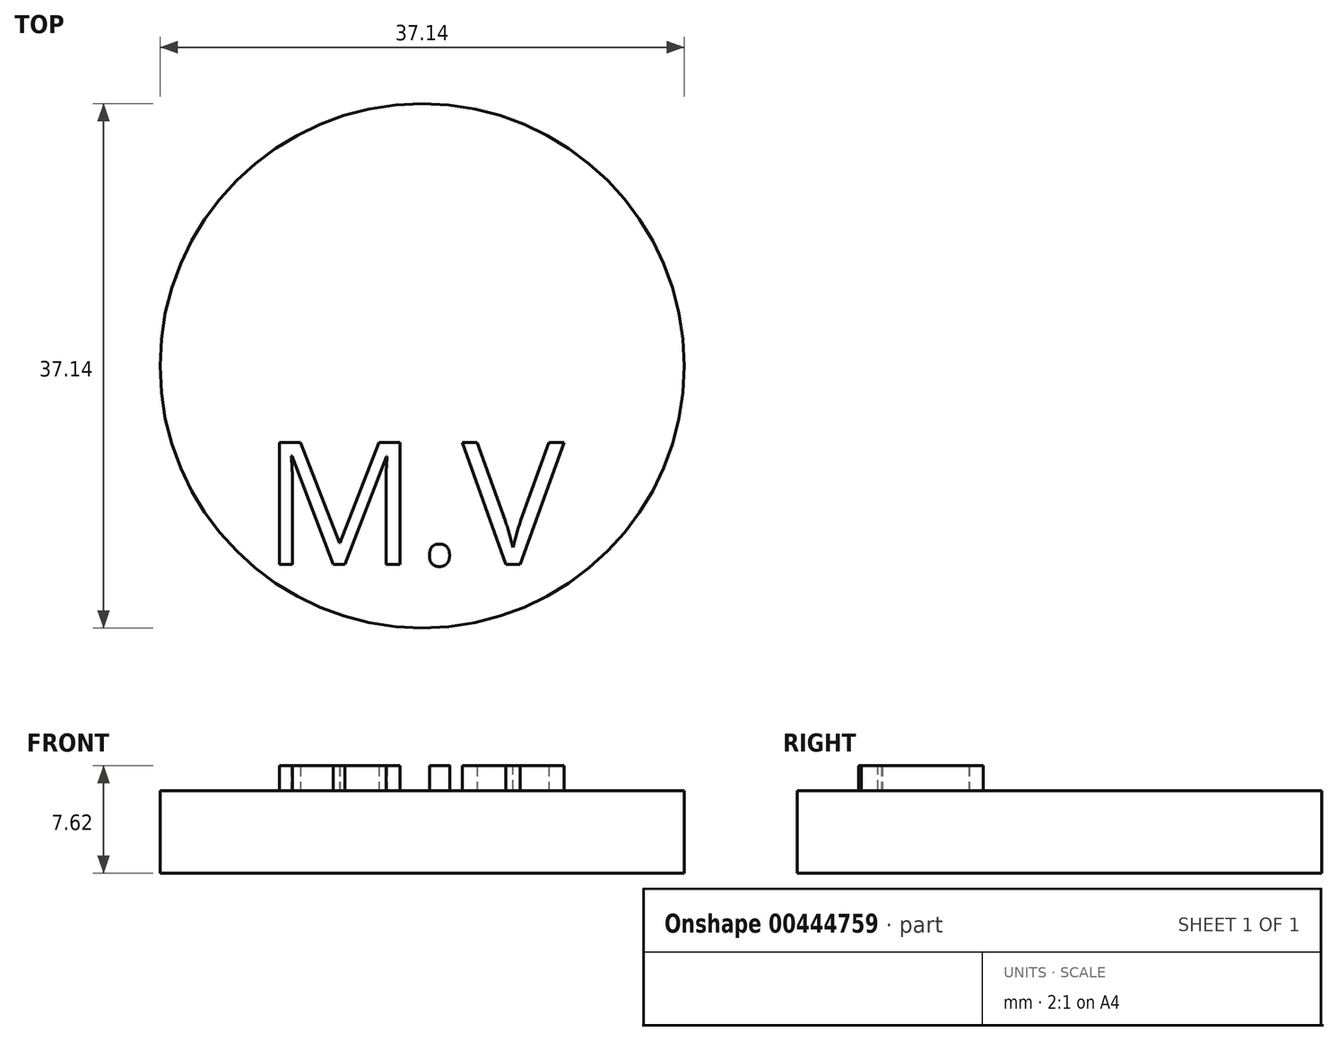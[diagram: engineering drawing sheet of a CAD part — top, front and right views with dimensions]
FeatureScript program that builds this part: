
annotation { "Feature Type Name" : "Feature", "Feature Type Description" : "" }
export const myFeature = defineFeature(function(context is Context, id is Id, definition is map)
    precondition{}
    {
        {
            var Q0;
            Q0=qCreatedBy(makeId("Top.planeOp"),FACE);
            var sketch = newSketch(context, id + "F0", { "sketchPlane" : qUnion([Q0])});
            skLineSegment(sketch, "E0.bottom", {"start": v(38.1, -19.05) * mm, "end": v(-38.1, -19.05) * mm});
            skLineSegment(sketch, "E0.top", {"start": v(38.1, 19.05) * mm, "end": v(-38.1, 19.05) * mm});
            skLineSegment(sketch, "E0.left", {"start": v(38.1, -19.05) * mm, "end": v(38.1, 19.05) * mm});
            skLineSegment(sketch, "E0.right", {"start": v(-38.1, -19.05) * mm, "end": v(-38.1, 19.05) * mm});
            skPoint(sketch, "E0.middle", {"position": v(0, 0) * mm});
            skSolve(sketch);
        }
        {
            var Q0;
            Q0=makeQuery(id+"F0.imprint","IMPRINT",FACE,{"disambiguationData":[TD([[makeQuery(id+"F0.imprint","IMPRINT",EDGE,{"derivedFrom":sQuery(id+"F0.wireOp",EDGE,"E0.bottom")}),-1.0]])]});
            var sketch = newSketch(context, id + "F1", { "sketchPlane" : qUnion([Q0])});
            skCircle(sketch, "E1", {"center": v(0, 0) * mm, "radius": 18.57 * mm});
            skSolve(sketch);
        }
        {
            var Q0;
            Q0=sQuery(id+"F0.wireOp",EDGE,"E0.top");
            var Q1;
            Q1=sQuery(id+"F0.wireOp",EDGE,"E0.right");
            var Q2;
            Q2=sQuery(id+"F0.wireOp",EDGE,"E0.bottom");
            var Q3;
            Q3=sQuery(id+"F0.wireOp",EDGE,"E0.left");
            extrude(context, id + "F2", {"bodyType" : ToolBodyType.SURFACE, "surfaceEntities" : qUnion([Q0, Q1, Q2, Q3]), "endBound" : BoundingType.SYMMETRIC, "depth" : 6.35 * mm});
        }
        {
            var Q0;
            Q0=makeQuery(id+"F1.imprint","IMPRINT",FACE,{"disambiguationData":[TD([[makeQuery(id+"F1.imprint","IMPRINT",EDGE,{"derivedFrom":sQuery(id+"F1.wireOp",EDGE,"E1")}),1.0]])]});
            extrude(context, id + "F3", {"entities" : qUnion([Q0]), "depth" : 5.84 * mm});
        }
        {
            var Q0;
            Q0=makeQuery(id+"F3.opExtrude","CAP_FACE",FACE,{"disambiguationData":[OSD([sQuery(id+"F1.wireOp",EDGE,"E1")])],"isStart":false});
            var sketch = newSketch(context, id + "F4", { "sketchPlane" : qUnion([Q0])});
            skCircle(sketch, "E2", {"center": v(0, 0) * mm, "radius": 6.17 * mm});
            skCircle(sketch, "E3", {"center": v(0, 0) * mm, "radius": 3.28 * mm});
            skSolve(sketch);
        }
        {
            var Q0;
            Q0=sQuery(id+"F4.wireOp",EDGE,"E2");
            var Q1;
            Q1=sQuery(id+"F4.wireOp",EDGE,"E3");
            extrude(context, id + "F5", {"bodyType" : ToolBodyType.SURFACE, "surfaceEntities" : qUnion([Q0, Q1]), "depth" : 2.54 * mm});
        }
        {
            var Q0;
            Q0=makeQuery(id+"F3.opExtrude","CAP_FACE",FACE,{"disambiguationData":[OSD([sQuery(id+"F1.wireOp",EDGE,"E1")])],"isStart":false});
            var sketch = newSketch(context, id + "F6", { "sketchPlane" : qUnion([Q0])});
            skLineSegment(sketch, "E4.bottom", {"start": v(18.47, -1.91) * mm, "end": v(-18.47, -1.91) * mm});
            skLineSegment(sketch, "E4.top", {"start": v(18.47, 1.91) * mm, "end": v(-18.47, 1.91) * mm});
            skLineSegment(sketch, "E4.left", {"start": v(18.47, -1.91) * mm, "end": v(18.47, 1.91) * mm});
            skLineSegment(sketch, "E4.right", {"start": v(-18.47, -1.91) * mm, "end": v(-18.47, 1.91) * mm});
            skPoint(sketch, "E4.middle", {"position": v(0, 0) * mm});
            skSolve(sketch);
        }
        {
            var Q0;
            Q0=sQuery(id+"F6.wireOp",EDGE,"E4.top");
            var Q1;
            Q1=sQuery(id+"F6.wireOp",EDGE,"E4.bottom");
            extrude(context, id + "F7", {"bodyType" : ToolBodyType.SURFACE, "surfaceEntities" : qUnion([Q0, Q1]), "depth" : 1.27 * mm, "hasSecondDirection" : true, "secondDirectionOppositeDirection" : true, "secondDirectionDepth" : 1.27 * mm});
        }
        {
            var Q0;
            Q0=qCreatedBy(makeId("Top.planeOp"),FACE);
            var sketch = newSketch(context, id + "F8", { "sketchPlane" : qUnion([Q0])});
            skText(sketch, "E5", { "text": "M.V", "fontName": "OpenSans-Regular.ttf"});
            const initialGuessF8  = {"E5": [-0.0113, -0.01405, 1, 0, 0.00871]};
            skSetInitialGuess(sketch, initialGuessF8);
            skSolve(sketch);
        }
        {
            var Q0;
            Q0 = qSketchRegion(id + "F8", true);
            extrude(context, id + "F9", {"entities" : qUnion([Q0]), "operationType" : NewBodyOperationType.ADD, "depth" : 7.62 * mm});
        }
        {
            var Q0;
            Q0=makeQuery(id+"F2.opExtrude","SWEPT_FACE",FACE,{"disambiguationData":[OSD([sQuery(id+"F0.wireOp",EDGE,"E0.top")])]});
            var Q1;
            Q1=makeQuery(id+"F2.opExtrude","SWEPT_FACE",FACE,{"disambiguationData":[OSD([sQuery(id+"F0.wireOp",EDGE,"E0.bottom")])]});
            chamfer(context, id + "F10", {"entities" : qUnion([Q0, Q1]), "width" : 5.08 * mm, "tangentPropagation" : true});
        }
    });
